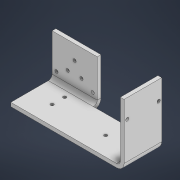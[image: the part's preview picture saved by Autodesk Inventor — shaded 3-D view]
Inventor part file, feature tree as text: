
AUTODESK INVENTOR PART (.ipt)
format: ipt  version: 2021 (Build 250183000, 183)  size: 216,064 bytes
history: native  units: mm
features: sheet_metal_op x9, sketch x7, other x4, hole x3, mirror x1, plane x1, split x1
ambient origin geometry x8: Origin, YZ Plane, XZ Plane, XY Plane, X Axis, Y Axis, Z Axis, Center Point
bodies: Solid1 (feature_tree)
feature tree (26):
  sheet_metal_op  "Face1"
  sheet_metal_op  "Flange1"
  sheet_metal_op  "Face2"
  sheet_metal_op  "Flange2"
  hole  "Hole1"  [1 undecoded]
  hole  "Hole2"  [1 undecoded]
  hole  "Hole3"  [1 undecoded]
  mirror  "Mirror1"
  plane  "Work Plane1"
  split  "Split1"
  sketch  "Sketch1"  dims[d0=72.0mm d1=36.0mm]
  other  "Plate1"
  sketch  "Sketch2"  dims[d2=72.0mm d3=36.0mm]
  other  "Plate2"
  sheet_metal_op  "Bend1"
  sheet_metal_op  "Corner1"
  sketch  "Sketch3"  dims[d4=6.0mm d5=6.0mm]
  other  "Plate3"
  sheet_metal_op  "Bend2"
  sketch  "Sketch4"  dims[d6=3.0mm]
  other  "Plate4"
  sheet_metal_op  "Bend3"
  sheet_metal_op  "Corner2"
  sketch  "Sketch5"  dims[d7=12.0mm]
  sketch  "Sketch6"  dims[d8=6.0mm]
  sketch  "Sketch7"  dims[d9=72.0mm d10=90.0deg d11=6.0mm d12=24.0mm d13=6.0mm d14=6.0mm d15=109.0mm d16=60.0mm d17=6.0mm d18=6.0mm d19=3.0mm d20=12.0mm d21=6.0mm d22=6.0mm d23=3.0mm d24=12.0mm d25=6.0mm d26=100.6mm d27=90.0deg d28=6.0mm d29=24.0mm d30=6.0mm d31=6.0mm d32=60.0mm d33=30.0mm d34=30.0mm d35=50.0mm d36=30.0mm d37=30.0mm d38=5.0mm d39=6.0mm d40=4.0mm d41=2.0mm d42=90.0deg d43=6.0mm d44=0.0mm d45=36.0mm d46=25.4mm d47=67.0mm d48=120.0deg d49=120.0deg d50=0.0mm d51=5.0mm d52=6.0mm d53=4.0mm d54=2.0mm d55=90.0deg d56=6.0mm d57=0.0mm d58=5.0mm d59=6.0mm d60=4.0mm d61=2.0mm d62=90.0deg d63=6.0mm d64=0.0mm d65=60.0mm d66=72.0mm d67=30.0mm d68=30.0mm d69=36.0mm d70=20.0mm d71=10.0mm d72=36.0mm d73=99.040396mm d74=49.520198mm]
note: 3 required parameter values undecoded (feature->parameter linkage not recoverable at this tier; creation-order binding heuristic only, values carry confidence <= 0.55)
